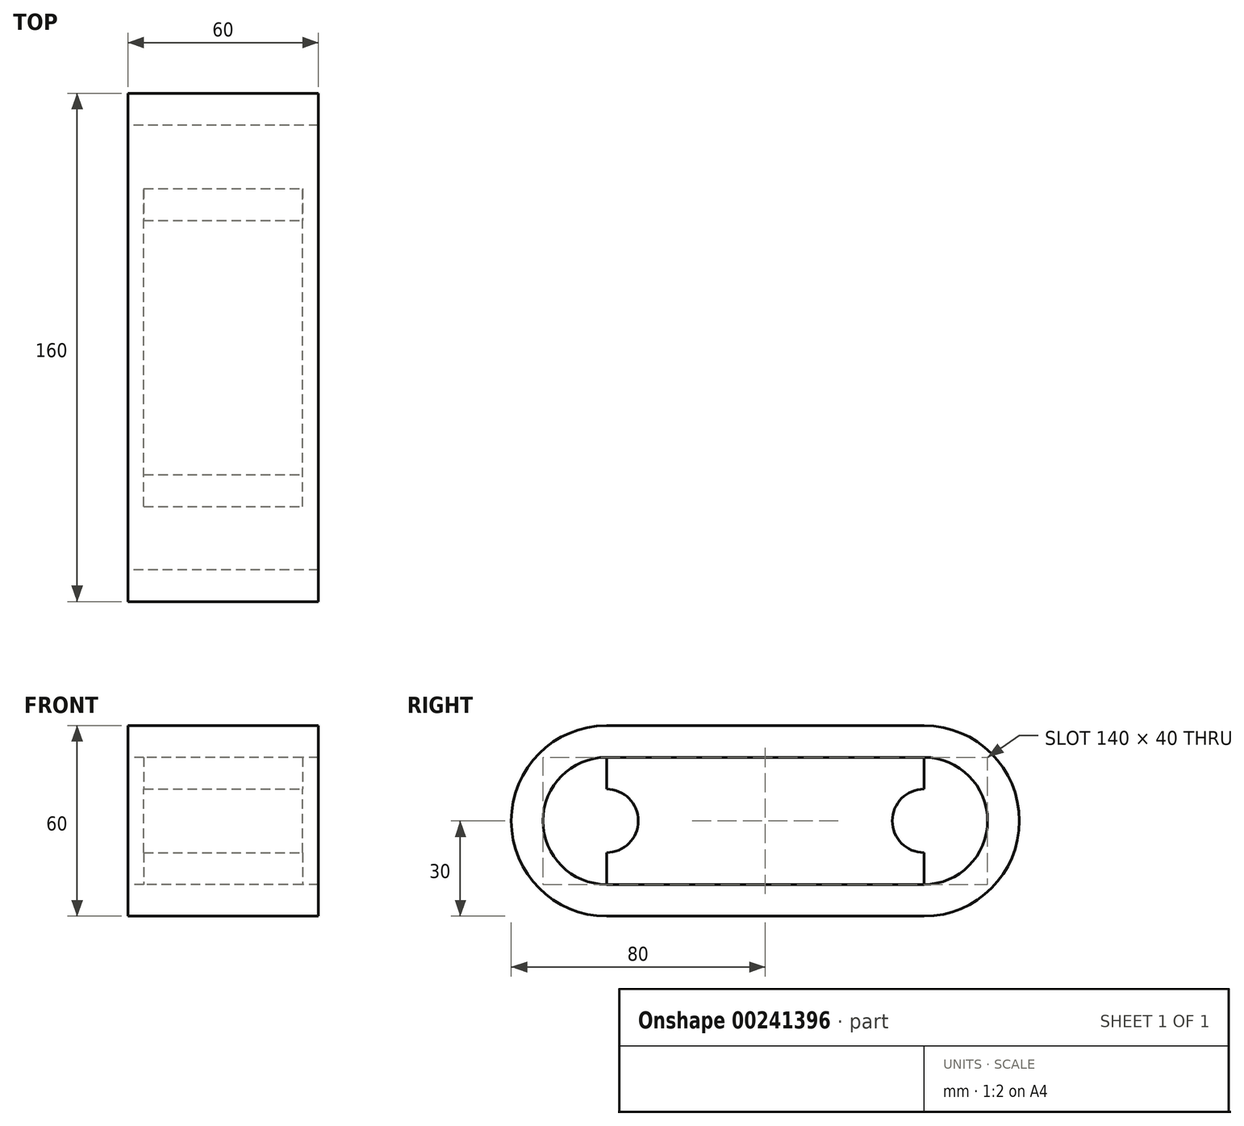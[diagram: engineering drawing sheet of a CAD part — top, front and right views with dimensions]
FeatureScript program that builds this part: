
annotation { "Feature Type Name" : "Feature", "Feature Type Description" : "" }
export const myFeature = defineFeature(function(context is Context, id is Id, definition is map)
    precondition{}
    {
        {
            var Q0;
            Q0=qCreatedBy(makeId("Right.planeOp"),FACE);
            var sketch = newSketch(context, id + "F0", { "sketchPlane" : qUnion([Q0])});
            skLineSegment(sketch, "E0.bottom", {"start": v(-50, 30) * mm, "end": v(50, 30) * mm});
            skLineSegment(sketch, "E0.top", {"start": v(-50, -30) * mm, "end": v(50, -30) * mm});
            skLineSegment(sketch, "E0.left", {"start": v(-50, 30) * mm, "end": v(-50, -30) * mm});
            skLineSegment(sketch, "E0.right", {"start": v(50, 30) * mm, "end": v(50, -30) * mm});
            skPoint(sketch, "E0.middle", {"position": v(0, 0) * mm});
            skLineSegment(sketch, "E1.bottom", {"start": v(-50, 20) * mm, "end": v(50, 20) * mm});
            skLineSegment(sketch, "E1.top", {"start": v(-50, -20) * mm, "end": v(50, -20) * mm});
            skLineSegment(sketch, "E1.left", {"start": v(-50, 20) * mm, "end": v(-50, -20) * mm});
            skLineSegment(sketch, "E1.right", {"start": v(50, 20) * mm, "end": v(50, -20) * mm});
            skArc(sketch, "E2", {"start": v(-50, 30) * mm, "mid": v(-80, 0) * mm, "end": v(-50, -30) * mm});
            skArc(sketch, "E3", {"start": v(-50, 20) * mm, "mid": v(-70, 0) * mm, "end": v(-50, -20) * mm});
            skArc(sketch, "E4", {"start": v(50, -30) * mm, "mid": v(80, 0) * mm, "end": v(50, 30) * mm});
            skArc(sketch, "E5", {"start": v(50, -20) * mm, "mid": v(70, 0) * mm, "end": v(50, 20) * mm});
            skSolve(sketch);
        }
        {
            var Q0;
            Q0 = qSketchRegion(id + "F0", true);
            extrude(context, id + "F1", {"entities" : qUnion([Q0]), "depth" : 60 * mm});
        }
        {
            var Q0;
            Q0=makeQuery(id+"F0.imprint","IMPRINT",FACE,{"disambiguationData":[TD([[makeQuery(id+"F0.imprint","IMPRINT",EDGE,{"derivedFrom":sQuery(id+"F0.wireOp",EDGE,"E1.bottom")}),-1.0]])]});
            var Q1;
            Q1=makeQuery(id+"F0.imprint","IMPRINT",FACE,{"disambiguationData":[TD([[makeQuery(id+"F0.imprint","IMPRINT",EDGE,{"derivedFrom":sQuery(id+"F0.wireOp",EDGE,"E1.right")}),1.0]])]});
            var Q2;
            Q2=makeQuery(id+"F0.imprint","IMPRINT",FACE,{"disambiguationData":[TD([[makeQuery(id+"F0.imprint","IMPRINT",EDGE,{"derivedFrom":sQuery(id+"F0.wireOp",EDGE,"E1.left")}),-1.0]])]});
            extrude(context, id + "F2", {"entities" : qUnion([Q0, Q1, Q2]), "operationType" : NewBodyOperationType.ADD, "depth" : 55 * mm, "hasSecondDirection" : true, "secondDirectionOppositeDirection" : true, "secondDirectionDepth" : -5 * mm});
        }
        {
            var Q0;
            Q0=makeQuery(id+"F2.opExtrude","CAP_FACE",FACE,{"disambiguationData":[OSD([sQuery(id+"F0.wireOp",EDGE,"E1.bottom"),sQuery(id+"F0.wireOp",EDGE,"E1.top"),sQuery(id+"F0.wireOp",EDGE,"E3"),sQuery(id+"F0.wireOp",EDGE,"E5")])],"isStart":false});
            var sketch = newSketch(context, id + "F3", { "sketchPlane" : qUnion([Q0])});
            skCircle(sketch, "E6", {"center": v(-50, 0) * mm, "radius": 10 * mm});
            skCircle(sketch, "E7", {"center": v(50, 0) * mm, "radius": 10 * mm});
            skSolve(sketch);
        }
        {
            var Q0;
            Q0 = qSketchRegion(id + "F3", true);
            extrude(context, id + "F4", {"entities" : qUnion([Q0]), "operationType" : NewBodyOperationType.REMOVE, "endBound" : BoundingType.THROUGH_ALL, "oppositeDirection" : true, "depth" : 25 * mm});
        }
    });
